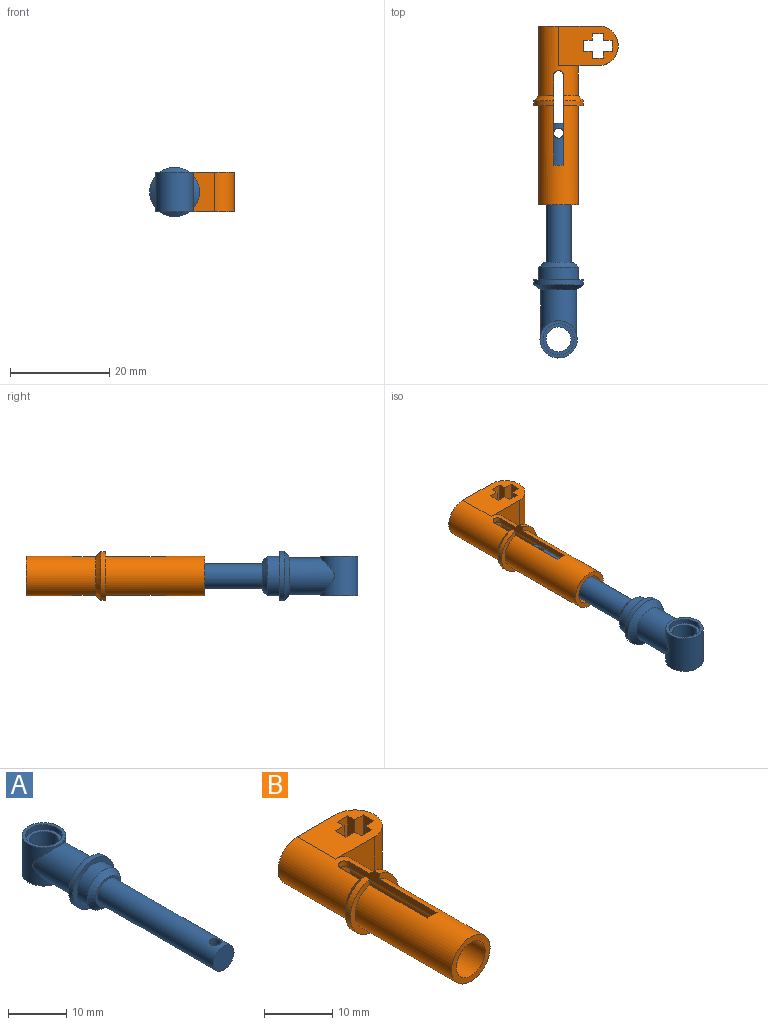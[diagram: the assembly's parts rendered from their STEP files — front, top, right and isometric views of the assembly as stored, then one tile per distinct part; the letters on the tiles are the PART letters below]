
ASSEMBLY  parts=2 mates=1
PART A: 18 faces, bbox 10x47.3x10 mm
  f0: cylinder r=2.5mm len=6mm, axis (0,0,1), area 94.2mm2, adj f13,f15
  f1: cylinder r=3.75mm len=8mm, axis (0,0,-1), area 138.3mm2, adj f2,f3,f4
  f2: plane 7.5x7.5mm, normal (0,0,1), area 13.5mm2, adj f1,f14
  f3: plane 7.5x7.5mm, normal (0,0,-1), area 13.5mm2, adj f1,f16
  f4: cylinder r=3.62mm len=9.04mm, axis (0,-1,0), area 169.3mm2, adj f1,f12
  f5: plane 5x5mm, normal (0,-1,0), area 19.6mm2, adj f6
  f6: cylinder r=2.5mm len=28mm, axis (0,-1,0), area 433.4mm2, adj f5,f7,f17
  f7: plane 6x6mm, normal (0,-1,0), area 8.6mm2, adj f6,f8
  f8: cone r=3mm half-angle=45deg, axis (0,1,0), area 31.1mm2, adj f7,f9
  f9: cylinder r=4mm len=8mm, axis (0,-1,0), area 62.8mm2, adj f8,f10
  f10: plane 10x10mm, normal (0,-1,0), area 28.3mm2, adj f9,f11
  f11: cylinder r=5mm len=10mm, axis (0,-1,0), area 31.4mm2, adj f10,f12
  f12: cone r=5mm half-angle=54deg, axis (0,-1,0), area 46.1mm2, adj f4,f11
  f13: plane 6.25x6.25mm, normal (0,0,1), area 11mm2, adj f0,f14
  f14: cylinder r=3.12mm len=6.25mm, axis (0,0,1), area 19.6mm2, adj f2,f13
  f15: plane 6.25x6.25mm, normal (0,0,-1), area 11mm2, adj f0,f16
  f16: cylinder r=3.12mm len=6.25mm, axis (0,0,-1), area 19.6mm2, adj f3,f15
  f17: cylinder r=1mm len=5mm, axis (0,0,1), area 30.1mm2, adj f6
PART B: 49 faces, bbox 17x36x9.8 mm
  f0: cylinder r=4mm len=14mm, axis (0,1,0), area 232mm2, adj f5,f6,f11,f12,f13,f15,f16,f18
  f1: cylinder r=3mm len=28mm, axis (0,1,0), area 451.2mm2, adj f7,f8,f12,f13,f14,f15,f16,f17
  f2: cylinder r=4mm len=20mm, axis (0,1,0), area 454.1mm2, adj f3,f8,f9,f12,f13,f14,f17,f18
  f3: plane 9.8x4mm, normal (0,-1,0), area 12.1mm2, adj f2,f4,f12,f18
  f4: cylinder r=5mm len=9.8mm, axis (0,1,0), area 13.7mm2, adj f3,f5,f12,f18
  f5: cone r=5mm half-angle=45deg, axis (0,-1,0), area 17.1mm2, adj f0,f4,f12,f18
  f6: plane 12x8mm, normal (0,1,0), area 70.1mm2, adj f0,f32,f34,f35,f36,f37,f38,f39
  f7: plane 6x6mm, normal (0,-1,0), area 28.3mm2, adj f1
  f8: plane 8x8mm, normal (0,-1,0), area 22mm2, adj f1,f2
  f9: plane 9.8x4mm, normal (0,-1,0), area 12.1mm2, adj f2,f10,f13,f19
  f10: cylinder r=5mm len=9.8mm, axis (0,1,0), area 13.7mm2, adj f9,f11,f13,f19
  f11: cone r=5mm half-angle=45deg, axis (0,-1,0), area 17.1mm2, adj f0,f10,f13,f19
  f12: plane 18.03x2.1mm, normal (1,0,0), area 20.3mm2, adj f0,f1,f2,f3,f4,f5,f14,f15
  f13: plane 18.03x2.1mm, normal (-1,0,0), area 20.3mm2, adj f0,f1,f2,f9,f10,f11,f14,f15
  f14: plane 2x1.17mm, normal (0,1,0), area 2mm2, adj f1,f2,f12,f13
  f15: cylinder r=1mm len=2mm, axis (0,0,1), area 3.3mm2, adj f0,f1,f12,f13
  f16: cylinder r=1mm len=2mm, axis (0,0,1), area 3.3mm2, adj f0,f1,f18,f19
  f17: plane 2x1.17mm, normal (0,1,0), area 2mm2, adj f1,f2,f18,f19
  f18: plane 18.03x2.1mm, normal (1,0,0), area 20.3mm2, adj f0,f1,f2,f3,f4,f5,f16,f17
  f19: plane 18.03x2.1mm, normal (-1,0,0), area 20.3mm2, adj f0,f1,f2,f9,f10,f11,f16,f17
  f20: plane 8x8mm, normal (0,-1,0), area 38.9mm2, adj f0,f32,f34,f35
  f21: plane 8x2.2mm, normal (1,0,0), area 17.6mm2, adj f22,f33,f34,f35
  f22: plane 8x1.8mm, normal (0,-1,0), area 14.4mm2, adj f21,f23,f34,f35
  f23: plane 8x1.4mm, normal (1,0,0), area 11.2mm2, adj f22,f24,f34,f35
  f24: plane 8x2.2mm, normal (0,-1,0), area 17.6mm2, adj f23,f25,f34,f35
  f25: plane 8x1.4mm, normal (-1,0,0), area 11.2mm2, adj f24,f26,f34,f35
  f26: plane 8x1.8mm, normal (0,-1,0), area 14.4mm2, adj f25,f27,f34,f35
  f27: plane 8x2.2mm, normal (-1,0,0), area 17.6mm2, adj f26,f28,f34,f35
  f28: plane 8x1.8mm, normal (0,1,0), area 14.4mm2, adj f27,f29,f34,f35
  f29: plane 8x1.4mm, normal (-1,0,0), area 11.2mm2, adj f28,f30,f34,f35
  f30: plane 8x2.2mm, normal (0,1,0), area 17.6mm2, adj f29,f31,f34,f35
  f31: plane 8x1.4mm, normal (1,0,0), area 11.2mm2, adj f30,f33,f34,f35
  f32: cylinder r=4mm len=8mm, axis (0,0,-1), area 100.5mm2, adj f6,f20,f34,f35
  f33: plane 8x1.8mm, normal (0,1,0), area 14.4mm2, adj f21,f31,f34,f35
  f34: plane 12x8mm, normal (0,0,1), area 70.2mm2, adj f0,f6,f20,f21,f22,f23,f24,f25
  f35: plane 12x8mm, normal (0,0,-1), area 70.2mm2, adj f0,f6,f20,f21,f22,f23,f24,f25
  f36: plane 7.75x2mm, normal (-1,0,0), area 15.5mm2, adj f6,f37,f47,f48
  f37: plane 7.75x3mm, normal (0,0,-1), area 23.2mm2, adj f6,f36,f38,f48
  f38: plane 7.75x1.5mm, normal (-1,0,0), area 11.6mm2, adj f6,f37,f39,f48
  f39: plane 7.75x2mm, normal (0,0,-1), area 15.5mm2, adj f6,f38,f40,f48
  f40: plane 7.75x1.5mm, normal (1,0,0), area 11.6mm2, adj f6,f39,f41,f48
  f41: plane 7.75x1.5mm, normal (0,0,-1), area 11.6mm2, adj f6,f40,f42,f48
  f42: plane 7.75x2mm, normal (1,0,0), area 15.5mm2, adj f6,f41,f43,f48
  f43: plane 7.75x1.5mm, normal (0,0,1), area 11.6mm2, adj f6,f42,f44,f48
  f44: plane 7.75x1.5mm, normal (1,0,0), area 11.6mm2, adj f6,f43,f45,f48
  f45: plane 7.75x2mm, normal (0,0,1), area 15.5mm2, adj f6,f44,f46,f48
  f46: plane 7.75x1.5mm, normal (-1,0,0), area 11.6mm2, adj f6,f45,f47,f48
  f47: plane 7.75x3mm, normal (0,0,1), area 23.2mm2, adj f6,f36,f46,f48
  f48: plane 6.5x5mm, normal (0,1,0), area 19mm2, adj f36,f37,f38,f39,f40,f41,f42,f43
PLACE A rot(axis=(0,0,-1),180deg) t=(-16.08,-30.92,15.52)mm
PLACE B rot(axis=(0.17,0.28,0.94),0deg) t=(-3.38,-47.36,15.52)mm fixed
MATE slider A.f4 <-> B.f0  axis (0,1,0) through (-3.38,-44.92,15.52)mm
